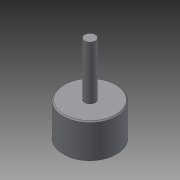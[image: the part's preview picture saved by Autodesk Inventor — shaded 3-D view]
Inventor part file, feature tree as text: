
AUTODESK INVENTOR PART (.ipt)
format: ipt  version: 2015 SP1 (Build 190203100, 203)  size: 91,648 bytes
history: native  units: in
note: dims shown in document units (in); Inventor stores cm internally (conversion verified against a paired STEP export)
features: revolve x1, chamfer x1
ambient origin geometry x8: Origin, YZ Plane, XZ Plane, XY Plane, X Axis, Y Axis, Z Axis, Center Point
bodies: Solid1 (feature_tree)
feature tree (2):
  revolve  "Revolution1"  [1 undecoded]
  chamfer  "Chamfer1"  Distance=2.5in
note: 1 required parameter value undecoded (feature->parameter linkage not recoverable at this tier; creation-order binding heuristic only, values carry confidence <= 0.55)
